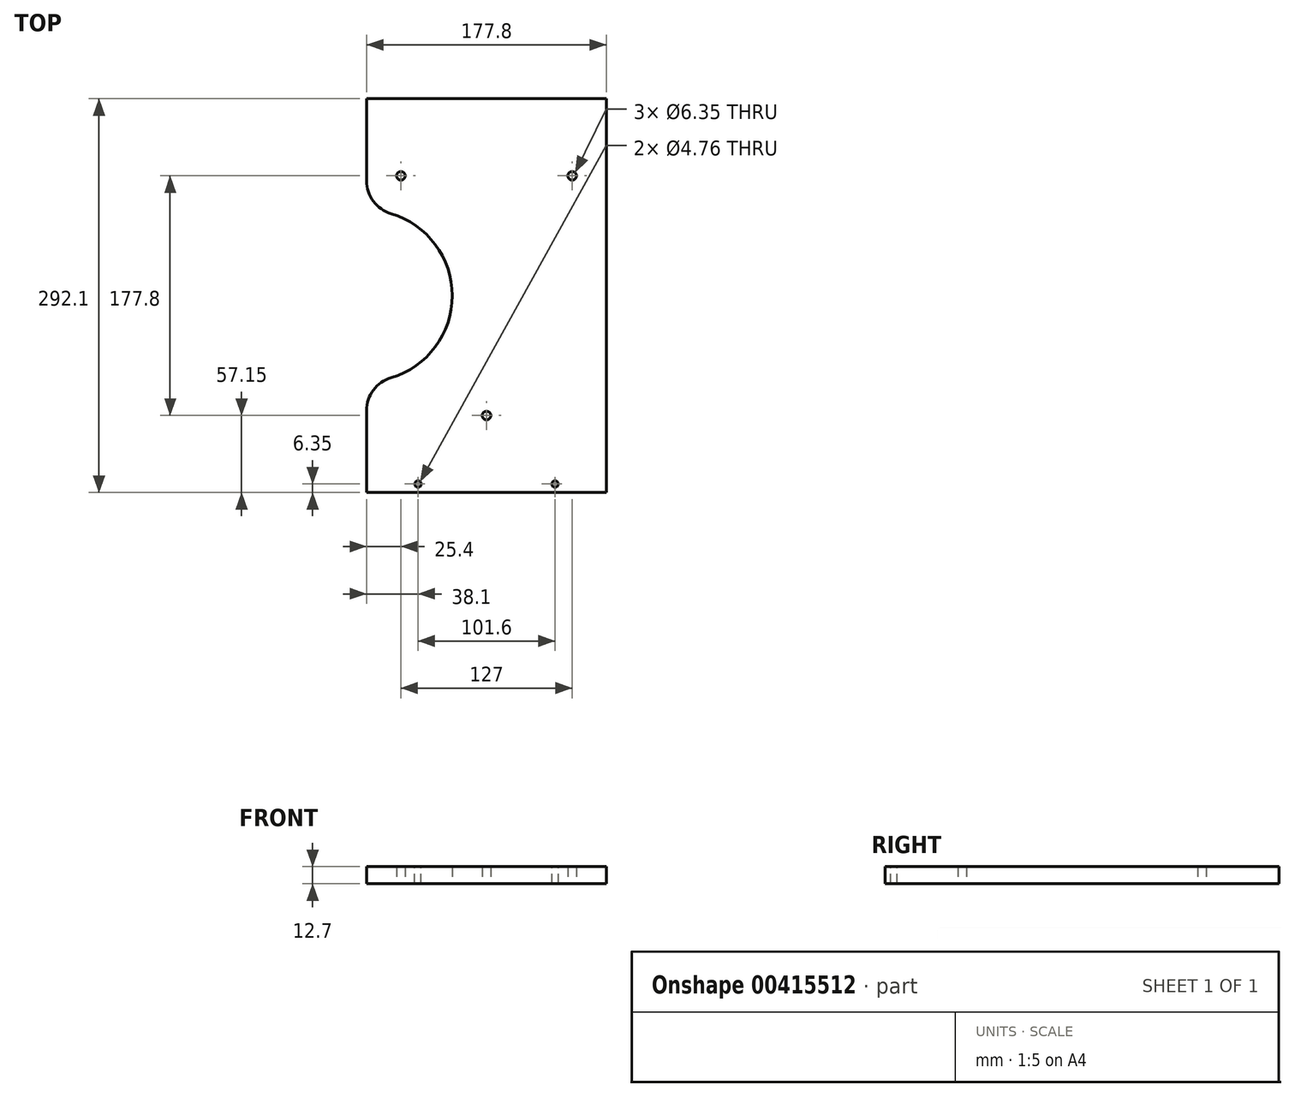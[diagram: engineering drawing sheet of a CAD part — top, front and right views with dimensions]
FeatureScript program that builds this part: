
annotation { "Feature Type Name" : "Feature", "Feature Type Description" : "" }
export const myFeature = defineFeature(function(context is Context, id is Id, definition is map)
    precondition{}
    {
        {
            var Q0;
            Q0=qCreatedBy(makeId("Top.planeOp"),FACE);
            var sketch = newSketch(context, id + "F0", { "sketchPlane" : qUnion([Q0])});
            skCircle(sketch, "E0", {"center": v(-63.5, 88.9) * mm, "radius": 3.18 * mm});
            skCircle(sketch, "E1", {"center": v(63.5, 88.9) * mm, "radius": 3.18 * mm});
            skCircle(sketch, "E2", {"center": v(0, -88.9) * mm, "radius": 3.18 * mm});
            skLineSegment(sketch, "E3", {"start": v(-63.5, 88.9) * mm, "end": v(63.5, 88.9) * mm, "construction": true});
            skLineSegment(sketch, "E4", {"start": v(0, 88.9) * mm, "end": v(0, -88.9) * mm, "construction": true});
            skLineSegment(sketch, "E5.bottom", {"start": v(88.9, 146.05) * mm, "end": v(-88.9, 146.05) * mm});
            skLineSegment(sketch, "E5.top", {"start": v(88.9, -146.05) * mm, "end": v(-88.9, -146.05) * mm});
            skLineSegment(sketch, "E5.left", {"start": v(88.9, 146.05) * mm, "end": v(88.9, -146.05) * mm});
            skLineSegment(sketch, "E5.right", {"start": v(-88.9, 146.05) * mm, "end": v(-88.9, -146.05) * mm});
            skPoint(sketch, "E5.middle", {"position": v(0, 0) * mm});
            skArc(sketch, "E6", {"start": v(-88.9, -63.5) * mm, "mid": v(-25.4, 0) * mm, "end": v(-88.9, 63.5) * mm});
            skSolve(sketch);
        }
        {
            var Q0;
            Q0=makeQuery(id+"F0.imprint","IMPRINT",FACE,{"disambiguationData":[TD([[makeQuery(id+"F0.imprint","IMPRINT",EDGE,{"derivedFrom":sQuery(id+"F0.wireOp",EDGE,"E0")}),-1.0]])]});
            extrude(context, id + "F1", {"entities" : qUnion([Q0]), "depth" : 12.7 * mm});
        }
        {
            var Q0;
            {var subQ0=sQuery(id+"F0.wireOp",EDGE,"E6");var subQ1=sQuery(id+"F0.wireOp",EDGE,"E5.right");Q0=makeQuery(id+"F1.opExtrude","SWEPT_EDGE",EDGE,{"disambiguationData":[OSD([subQ1,subQ0]),TDD([makeQuery(id+"F0.imprint","INTERSECT",VERTEX,{"disambiguationData":[OD(1.0)],"derivedFrom":[subQ1,subQ0]})])]});}
            var Q1;
            {var subQ0=sQuery(id+"F0.wireOp",EDGE,"E6");var subQ1=sQuery(id+"F0.wireOp",EDGE,"E5.right");Q1=makeQuery(id+"F1.opExtrude","SWEPT_EDGE",EDGE,{"disambiguationData":[OSD([subQ1,subQ0]),TDD([makeQuery(id+"F0.imprint","INTERSECT",VERTEX,{"disambiguationData":[OD(0.0)],"derivedFrom":[subQ1,subQ0]})])]});}
            fillet(context, id + "F2", {"entities" : qUnion([Q0, Q1]), "radius" : 25.4 * mm, "tangentPropagation" : true, "allowEdgeOverflow" : false});
        }
        {
            var Q0;
            Q0=makeQuery(id+"F1.opExtrude","CAP_FACE",FACE,{"disambiguationData":[OSD([sQuery(id+"F0.wireOp",EDGE,"E0"),sQuery(id+"F0.wireOp",EDGE,"E1"),sQuery(id+"F0.wireOp",EDGE,"E2"),sQuery(id+"F0.wireOp",EDGE,"E5.bottom"),sQuery(id+"F0.wireOp",EDGE,"E5.top"),sQuery(id+"F0.wireOp",EDGE,"E5.left"),sQuery(id+"F0.wireOp",EDGE,"E5.right"),sQuery(id+"F0.wireOp",EDGE,"E6")])],"isStart":false});
            var sketch = newSketch(context, id + "F3", { "sketchPlane" : qUnion([Q0])});
            skCircle(sketch, "E7", {"center": v(-50.8, -139.7) * mm, "radius": 2.38 * mm});
            skCircle(sketch, "E8", {"center": v(50.8, -139.7) * mm, "radius": 2.38 * mm});
            skLineSegment(sketch, "E9", {"start": v(-50.8, -139.7) * mm, "end": v(50.8, -139.7) * mm, "construction": true});
            skLineSegment(sketch, "E10", {"start": v(0, 0) * mm, "end": v(0, -139.7) * mm, "construction": true});
            skSolve(sketch);
        }
        {
            var Q0;
            Q0=qSketchRegion(id+"F3",true);
            extrude(context, id + "F4", {"entities" : qUnion([Q0]), "operationType" : NewBodyOperationType.REMOVE, "endBound" : BoundingType.THROUGH_ALL, "oppositeDirection" : true, "depth" : 25.4 * mm});
        }
    });
